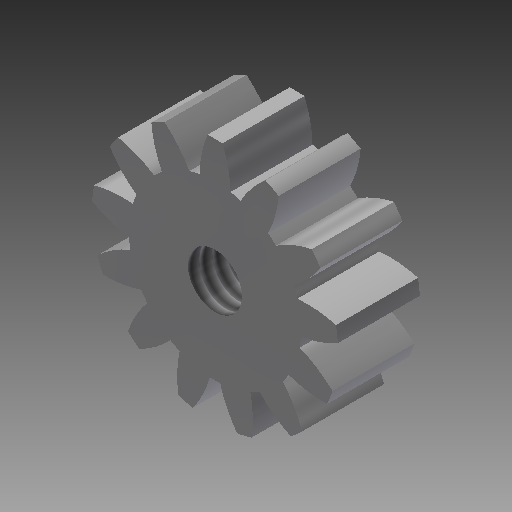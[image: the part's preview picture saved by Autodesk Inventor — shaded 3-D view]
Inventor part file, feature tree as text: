
AUTODESK INVENTOR PART (.ipt)
format: ipt  version: 2017 (Build 210142000, 142)  size: 214,016 bytes
history: native  units: mm (DEFAULTED — no unit token found)
features: plane x3, other x3, sketch x3, extrude x1, hole x1
ambient origin geometry x8: Origin, YZ Plane, XZ Plane, XY Plane, X Axis, Y Axis, Z Axis, Center Point
bodies: Solid1 (feature_tree)
feature tree (11):
  extrude  "Extrusion1"  Depth=5.0mm TaperAngle=0.0deg
  plane  "Work Plane2"
  plane  "Work Plane8"
  plane  "Work Plane9"
  other  "Spur Gear"
  hole  "Hole1"  [1 undecoded]
  sketch  "Sketch1"  dims[d0=15.0mm d1=5.0mm d2=0.0mm]
  sketch  "Sketch2"  dims[d3=13.0mm d4=10.0mm d5=0.0mm]
  other  "Srf1"
  sketch  "Sketch3"  dims[d16=24.5mm d17=0.0mm d34=2.41661mm d39=0.0mm d41=0.0mm d43=24.5mm d46=24.5mm d47=0.0mm d48=0.0mm d49=3.302mm d50=8.331mm d51=4.0mm d52=2.0mm d53=90.0deg d54=12.3mm d55=20.594885mm]
  other  "Pitch Diameter"
note: 1 required parameter value undecoded (feature->parameter linkage not recoverable at this tier; creation-order binding heuristic only, values carry confidence <= 0.55)
